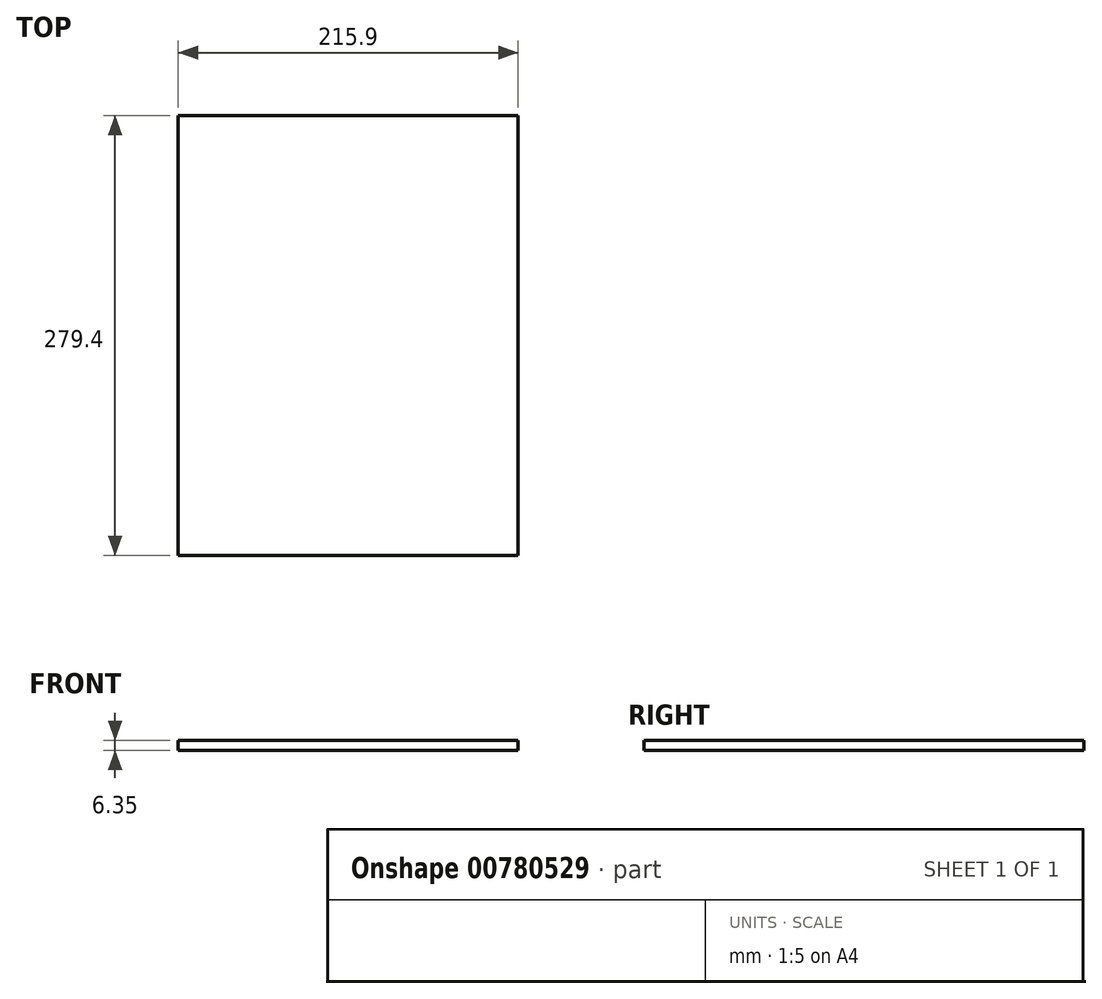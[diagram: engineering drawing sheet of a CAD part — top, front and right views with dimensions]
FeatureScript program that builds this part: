
annotation { "Feature Type Name" : "Feature", "Feature Type Description" : "" }
export const myFeature = defineFeature(function(context is Context, id is Id, definition is map)
    precondition{}
    {
        {
            var Q0;
            Q0=qCreatedBy(makeId("Top.planeOp"),FACE);
            var sketch = newSketch(context, id + "F0", { "sketchPlane" : qUnion([Q0])});
            skLineSegment(sketch, "E0.bottom", {"start": v(107.95, -139.7) * mm, "end": v(-107.95, -139.7) * mm});
            skLineSegment(sketch, "E0.top", {"start": v(107.95, 139.7) * mm, "end": v(-107.95, 139.7) * mm});
            skLineSegment(sketch, "E0.left", {"start": v(107.95, -139.7) * mm, "end": v(107.95, 139.7) * mm});
            skLineSegment(sketch, "E0.right", {"start": v(-107.95, -139.7) * mm, "end": v(-107.95, 139.7) * mm});
            skPoint(sketch, "E0.middle", {"position": v(0, 0) * mm});
            skSolve(sketch);
        }
        {
            var Q0;
            Q0 = qSketchRegion(id + "F0", true);
            extrude(context, id + "F1", {"entities" : qUnion([Q0]), "depth" : 6.35 * mm, "offsetDistance" : 25.4 * mm});
        }
    });
